# Revit family: ef-35_60uct(40)2_udt(40a)2_uet(40a)2_uft(40a)2_ugt(40a)2_50Hz
name_source: partatom
category: 機械設備
units: mm (PartAtom-declared; Revit-internal decimal feet)

## family parameters
OmniClass タイトル = Industrial Ventilating Equipment
OmniClass 番号 = 23.75.35.21.17
パーツ タイプ = 標準
ロード時にボイドで切り取り = はい
丸型コネクタ寸法 = 直径を使用
作業面ベース = いいえ
共有 = いいえ
常に垂直 = はい
部屋計算ポイント = はい

## types (25) — shared parameters
IfcExportAs = IfcFanType
IfcExportType = TUBEAXIAL
MID風量 = 0.0 m³/h
MIN風量 = 0.0 m³/h
OmniClassCode = 23-33 31 19 11 17
URL = https://www.mitsubishielectric.co.jp
Uniclass2015Code = Pr_65_67_29_67
Uniclass2015Title = Propeller fans
Uniclass2015Version = Systems v1.9
ファンの種類 = 軸流羽根
フレームの厚さ = 10  [stored 0.0328084 ft]
仕様書バージョン = Version1.0
企業コード = 108420
分類コード = 50052503100110
周波数 = 50 Hz
呼称 = 有圧扇
極 = 4
極数 = 3
法定耐用年数 = 15
相 = 3
製品リリース年月 = 2022年6月1日
製品出荷対象 = 国内
製造元 = 三菱電機株式会社
設置方法 = 壁付
説明 = 産業用有圧換気扇 機器冷却用 排気専用
負荷分類 = 3_ファン類
運転質量 = 0.00 kg

## per-type parameters (varying)
| type | Depth | Height | MAX風量 | Width | オリフィス_Depth | オリフィス径 | モデル | モーター径 | モーター表示 | レグ_Depth | レグ_Height | レグ_Width | 価格 | 消費電力 | 羽根径 | 製品質量 | 質量 | 銘板_H | 銘板_Height | 銘板_Width | 銘板表示 | 電動機出力 | 電圧 |
| EF-35UCT2_200V | 171  [stored 0.561024 ft] | 470  [stored 1.54199 ft] | 2500.0 m³/h | 470  [stored 1.54199 ft] | 70  [stored 0.229659 ft] | 415  [stored 1.36155 ft] | EF-35UCT2 | 5  [stored 0.0164042 ft] | いいえ | 143 | 387  [stored 1.26969 ft] | 387  [stored 1.26969 ft] | 78400 $ | 90 W | ∅350 | 6.80 kg | 8.16 kg | 60  [stored 0.19685 ft] | 153  [stored 0.501969 ft] | 120  [stored 0.393701 ft] | はい | 100 W | 200 V |
| EF-35UDT2_200V | 221  [stored 0.725066 ft] | 470  [stored 1.54199 ft] | 3000.0 m³/h | 470  [stored 1.54199 ft] | 70  [stored 0.229659 ft] | 415  [stored 1.36155 ft] | EF-35UDT2 | 5  [stored 0.0164042 ft] | いいえ | 189  [stored 0.620079 ft] | 386  [stored 1.2664 ft] | 386  [stored 1.2664 ft] | 86000 $ | 140 W | ∅350 | 9.20 kg | 11.04 kg | 80  [stored 0.262467 ft] | 181  [stored 0.593832 ft] | 147  [stored 0.482283 ft] | はい | 150 W | 200 V |
| EF-40UET2_200V | 222 | 520  [stored 1.70604 ft] | 4800.0 m³/h | 520  [stored 1.70604 ft] | 80  [stored 0.262467 ft] | 490  [stored 1.60761 ft] | EF-40UET2 | 131  [stored 0.42979 ft] | はい | 196  [stored 0.643045 ft] | 400  [stored 1.31234 ft] | 400  [stored 1.31234 ft] | 109000 $ | 245 W | ∅400 | 13.20 kg | 15.84 kg | 5  [stored 0.0164042 ft] | 5  [stored 0.0164042 ft] | 5  [stored 0.0164042 ft] | いいえ | 400 W | 200 V |
| EF-50UFT2_200V | 258  [stored 0.846457 ft] | 620  [stored 2.03412 ft] | 7200.0 m³/h | 620  [stored 2.03412 ft] | 95 | 605  [stored 1.98491 ft] | EF-50UFT2 | 131  [stored 0.42979 ft] | はい | 232  [stored 0.761155 ft] | 503 | 503 | 138000 $ | 370 W | ∅500 | 19.50 kg | 23.40 kg | 5  [stored 0.0164042 ft] | 5  [stored 0.0164042 ft] | 5  [stored 0.0164042 ft] | いいえ | 750 W | 200 V |
| EF-60UGT2_200V | 266  [stored 0.872703 ft] | 710 | 11500.0 m³/h | 710 | 100  [stored 0.328084 ft] | 705  [stored 2.31299 ft] | EF-60UGT2 | 163  [stored 0.534777 ft] | はい | 230  [stored 0.754593 ft] | 598 | 598 | 203000 $ | 680 W | ∅600 | 26.40 kg | 31.68 kg | 5  [stored 0.0164042 ft] | 5  [stored 0.0164042 ft] | 5  [stored 0.0164042 ft] | いいえ | 1500 W | 200 V |
| EF-35UCT2_220V | 171  [stored 0.561024 ft] | 470  [stored 1.54199 ft] | 2500.0 m³/h | 470  [stored 1.54199 ft] | 70  [stored 0.229659 ft] | 415  [stored 1.36155 ft] | EF-35UCT2 | 5  [stored 0.0164042 ft] | いいえ | 143 | 387  [stored 1.26969 ft] | 387  [stored 1.26969 ft] | 78400 $ | 110 W | ∅350 | 6.80 kg | 8.16 kg | 60  [stored 0.19685 ft] | 153  [stored 0.501969 ft] | 120  [stored 0.393701 ft] | はい | 100 W | 220 V |
| EF-35UDT2_220V | 221  [stored 0.725066 ft] | 470  [stored 1.54199 ft] | 3000.0 m³/h | 470  [stored 1.54199 ft] | 70  [stored 0.229659 ft] | 415  [stored 1.36155 ft] | EF-35UDT2 | 5  [stored 0.0164042 ft] | いいえ | 189  [stored 0.620079 ft] | 386  [stored 1.2664 ft] | 386  [stored 1.2664 ft] | 86000 $ | 155 W | ∅350 | 9.20 kg | 11.04 kg | 80  [stored 0.262467 ft] | 181  [stored 0.593832 ft] | 147  [stored 0.482283 ft] | はい | 150 W | 220 V |
| EF-40UET2_220V | 222 | 520  [stored 1.70604 ft] | 4800.0 m³/h | 520  [stored 1.70604 ft] | 80  [stored 0.262467 ft] | 490  [stored 1.60761 ft] | EF-40UET2 | 131  [stored 0.42979 ft] | はい | 196  [stored 0.643045 ft] | 400  [stored 1.31234 ft] | 400  [stored 1.31234 ft] | 109000 $ | 273 W | ∅400 | 13.20 kg | 15.84 kg | 5  [stored 0.0164042 ft] | 5  [stored 0.0164042 ft] | 5  [stored 0.0164042 ft] | いいえ | 400 W | 220 V |
| EF-50UFT2_220V | 258  [stored 0.846457 ft] | 620  [stored 2.03412 ft] | 7200.0 m³/h | 620  [stored 2.03412 ft] | 95 | 605  [stored 1.98491 ft] | EF-50UFT2 | 131  [stored 0.42979 ft] | はい | 232  [stored 0.761155 ft] | 503 | 503 | 138000 $ | 400 W | ∅500 | 19.50 kg | 23.40 kg | 5  [stored 0.0164042 ft] | 5  [stored 0.0164042 ft] | 5  [stored 0.0164042 ft] | いいえ | 750 W | 220 V |
| EF-60UGT2_220V | 266  [stored 0.872703 ft] | 710 | 11500.0 m³/h | 710 | 100  [stored 0.328084 ft] | 705  [stored 2.31299 ft] | EF-60UGT2 | 163  [stored 0.534777 ft] | はい | 230  [stored 0.754593 ft] | 598 | 598 | 203000 $ | 730 W | ∅600 | 26.40 kg | 31.68 kg | 5  [stored 0.0164042 ft] | 5  [stored 0.0164042 ft] | 5  [stored 0.0164042 ft] | いいえ | 1500 W | 220 V |
| EF-35UCT40A2_380V | 171  [stored 0.561024 ft] | 470  [stored 1.54199 ft] | 2500.0 m³/h | 470  [stored 1.54199 ft] | 70  [stored 0.229659 ft] | 415  [stored 1.36155 ft] | EF-35UCT40A2 | 5  [stored 0.0164042 ft] | いいえ | 143 | 387  [stored 1.26969 ft] | 387  [stored 1.26969 ft] | 86600 $ | 84 W | ∅350 | 6.80 kg | 8.16 kg | 60  [stored 0.19685 ft] | 153  [stored 0.501969 ft] | 120  [stored 0.393701 ft] | はい | 100 W | 380 V |
| EF-35UDT40A2_380V | 221  [stored 0.725066 ft] | 470  [stored 1.54199 ft] | 3000.0 m³/h | 470  [stored 1.54199 ft] | 70  [stored 0.229659 ft] | 415  [stored 1.36155 ft] | EF-35UDT40A2 | 5  [stored 0.0164042 ft] | いいえ | 189  [stored 0.620079 ft] | 386  [stored 1.2664 ft] | 386  [stored 1.2664 ft] | 94900 $ | 136 W | ∅350 | 9.20 kg | 11.04 kg | 80  [stored 0.262467 ft] | 181  [stored 0.593832 ft] | 147  [stored 0.482283 ft] | はい | 150 W | 380 V |
| EF-40UET40A2_380V | 222 | 520  [stored 1.70604 ft] | 4800.0 m³/h | 520  [stored 1.70604 ft] | 80  [stored 0.262467 ft] | 490  [stored 1.60761 ft] | EF-40UET40A2 | 131  [stored 0.42979 ft] | はい | 196  [stored 0.643045 ft] | 400  [stored 1.31234 ft] | 400  [stored 1.31234 ft] | 121000 $ | 265 W | ∅400 | 13.20 kg | 15.84 kg | 5  [stored 0.0164042 ft] | 5  [stored 0.0164042 ft] | 5  [stored 0.0164042 ft] | いいえ | 400 W | 380 V |
| EF-50UFT40A2_380V | 258  [stored 0.846457 ft] | 620  [stored 2.03412 ft] | 7200.0 m³/h | 620  [stored 2.03412 ft] | 95 | 605  [stored 1.98491 ft] | EF-50UFT40A2 | 131  [stored 0.42979 ft] | はい | 232  [stored 0.761155 ft] | 503 | 503 | 151000 $ | 345 W | ∅500 | 19.50 kg | 23.40 kg | 5  [stored 0.0164042 ft] | 5  [stored 0.0164042 ft] | 5  [stored 0.0164042 ft] | いいえ | 750 W | 380 V |
| EF-60UGT40A2_380V | 266  [stored 0.872703 ft] | 710 | 11500.0 m³/h | 710 | 100  [stored 0.328084 ft] | 705  [stored 2.31299 ft] | EF-60UGT40A2 | 163  [stored 0.534777 ft] | はい | 230  [stored 0.754593 ft] | 598 | 598 | 223000 $ | 695 W | ∅600 | 26.40 kg | 31.68 kg | 5  [stored 0.0164042 ft] | 5  [stored 0.0164042 ft] | 5  [stored 0.0164042 ft] | いいえ | 1500 W | 380 V |
| EF-35UCT40A2_400V | 171  [stored 0.561024 ft] | 470  [stored 1.54199 ft] | 2500.0 m³/h | 470  [stored 1.54199 ft] | 70  [stored 0.229659 ft] | 415  [stored 1.36155 ft] | EF-35UCT40A2 | 5  [stored 0.0164042 ft] | いいえ | 143 | 387  [stored 1.26969 ft] | 387  [stored 1.26969 ft] | 86600 $ | 89 W | ∅350 | 6.80 kg | 8.16 kg | 60  [stored 0.19685 ft] | 153  [stored 0.501969 ft] | 120  [stored 0.393701 ft] | はい | 100 W | 400 V |
| EF-35UDT40A2_400V | 221  [stored 0.725066 ft] | 470  [stored 1.54199 ft] | 3000.0 m³/h | 470  [stored 1.54199 ft] | 70  [stored 0.229659 ft] | 415  [stored 1.36155 ft] | EF-35UDT40A2 | 5  [stored 0.0164042 ft] | いいえ | 189  [stored 0.620079 ft] | 386  [stored 1.2664 ft] | 386  [stored 1.2664 ft] | 94900 $ | 145 W | ∅350 | 9.20 kg | 11.04 kg | 80  [stored 0.262467 ft] | 181  [stored 0.593832 ft] | 147  [stored 0.482283 ft] | はい | 150 W | 400 V |
| EF-40UET40A2_400V | 222 | 520  [stored 1.70604 ft] | 4800.0 m³/h | 520  [stored 1.70604 ft] | 80  [stored 0.262467 ft] | 490  [stored 1.60761 ft] | EF-40UET40A2 | 131  [stored 0.42979 ft] | はい | 196  [stored 0.643045 ft] | 400  [stored 1.31234 ft] | 400  [stored 1.31234 ft] | 121000 $ | 275 W | ∅400 | 13.20 kg | 15.84 kg | 5  [stored 0.0164042 ft] | 5  [stored 0.0164042 ft] | 5  [stored 0.0164042 ft] | いいえ | 400 W | 400 V |
| EF-50UFT40A2_400V | 258  [stored 0.846457 ft] | 620  [stored 2.03412 ft] | 7200.0 m³/h | 620  [stored 2.03412 ft] | 95 | 605  [stored 1.98491 ft] | EF-50UFT40A2 | 131  [stored 0.42979 ft] | はい | 232  [stored 0.761155 ft] | 503 | 503 | 151000 $ | 365 W | ∅500 | 19.50 kg | 23.40 kg | 5  [stored 0.0164042 ft] | 5  [stored 0.0164042 ft] | 5  [stored 0.0164042 ft] | いいえ | 750 W | 400 V |
| EF-60UGT40A2_400V | 266  [stored 0.872703 ft] | 710 | 11500.0 m³/h | 710 | 100  [stored 0.328084 ft] | 705  [stored 2.31299 ft] | EF-60UGT40A2 | 163  [stored 0.534777 ft] | はい | 230  [stored 0.754593 ft] | 598 | 598 | 223000 $ | 695 W | ∅600 | 26.40 kg | 31.68 kg | 5  [stored 0.0164042 ft] | 5  [stored 0.0164042 ft] | 5  [stored 0.0164042 ft] | いいえ | 1500 W | 400 V |
| EF-35UCT40A2_415V | 171  [stored 0.561024 ft] | 470  [stored 1.54199 ft] | 2500.0 m³/h | 470  [stored 1.54199 ft] | 70  [stored 0.229659 ft] | 415  [stored 1.36155 ft] | EF-35UCT40A2 | 5  [stored 0.0164042 ft] | いいえ | 143 | 387  [stored 1.26969 ft] | 387  [stored 1.26969 ft] | 86600 $ | 95 W | ∅350 | 6.80 kg | 8.16 kg | 60  [stored 0.19685 ft] | 153  [stored 0.501969 ft] | 120  [stored 0.393701 ft] | はい | 100 W | 415 V |
| EF-35UDT40A2_415V | 221  [stored 0.725066 ft] | 470  [stored 1.54199 ft] | 3000.0 m³/h | 470  [stored 1.54199 ft] | 70  [stored 0.229659 ft] | 415  [stored 1.36155 ft] | EF-35UDT40A2 | 5  [stored 0.0164042 ft] | いいえ | 189  [stored 0.620079 ft] | 386  [stored 1.2664 ft] | 386  [stored 1.2664 ft] | 94900 $ | 150 W | ∅350 | 9.20 kg | 11.04 kg | 80  [stored 0.262467 ft] | 181  [stored 0.593832 ft] | 147  [stored 0.482283 ft] | はい | 150 W | 415 V |
| EF-40UET40A2_415V | 222 | 520  [stored 1.70604 ft] | 4800.0 m³/h | 520  [stored 1.70604 ft] | 80  [stored 0.262467 ft] | 490  [stored 1.60761 ft] | EF-40UET40A2 | 131  [stored 0.42979 ft] | はい | 196  [stored 0.643045 ft] | 400  [stored 1.31234 ft] | 400  [stored 1.31234 ft] | 121000 $ | 285 W | ∅400 | 13.20 kg | 15.84 kg | 5  [stored 0.0164042 ft] | 5  [stored 0.0164042 ft] | 5  [stored 0.0164042 ft] | いいえ | 400 W | 415 V |
| EF-50UFT40A2_415V | 258  [stored 0.846457 ft] | 620  [stored 2.03412 ft] | 7200.0 m³/h | 620  [stored 2.03412 ft] | 95 | 605  [stored 1.98491 ft] | EF-50UFT40A2 | 131  [stored 0.42979 ft] | はい | 232  [stored 0.761155 ft] | 503 | 503 | 151000 $ | 375 W | ∅500 | 19.50 kg | 23.40 kg | 5  [stored 0.0164042 ft] | 5  [stored 0.0164042 ft] | 5  [stored 0.0164042 ft] | いいえ | 750 W | 415 V |
| EF-60UGT40A2_415V | 266  [stored 0.872703 ft] | 710 | 11500.0 m³/h | 710 | 100  [stored 0.328084 ft] | 705  [stored 2.31299 ft] | EF-60UGT40A2 | 163  [stored 0.534777 ft] | はい | 230  [stored 0.754593 ft] | 598 | 598 | 223000 $ | 735 W | ∅600 | 26.40 kg | 31.68 kg | 5  [stored 0.0164042 ft] | 5  [stored 0.0164042 ft] | 5  [stored 0.0164042 ft] | いいえ | 1500 W | 415 V |

note: [stored X ft] marks values corroborated as IEEE doubles in the binary element streams (Revit-internal decimal feet)
